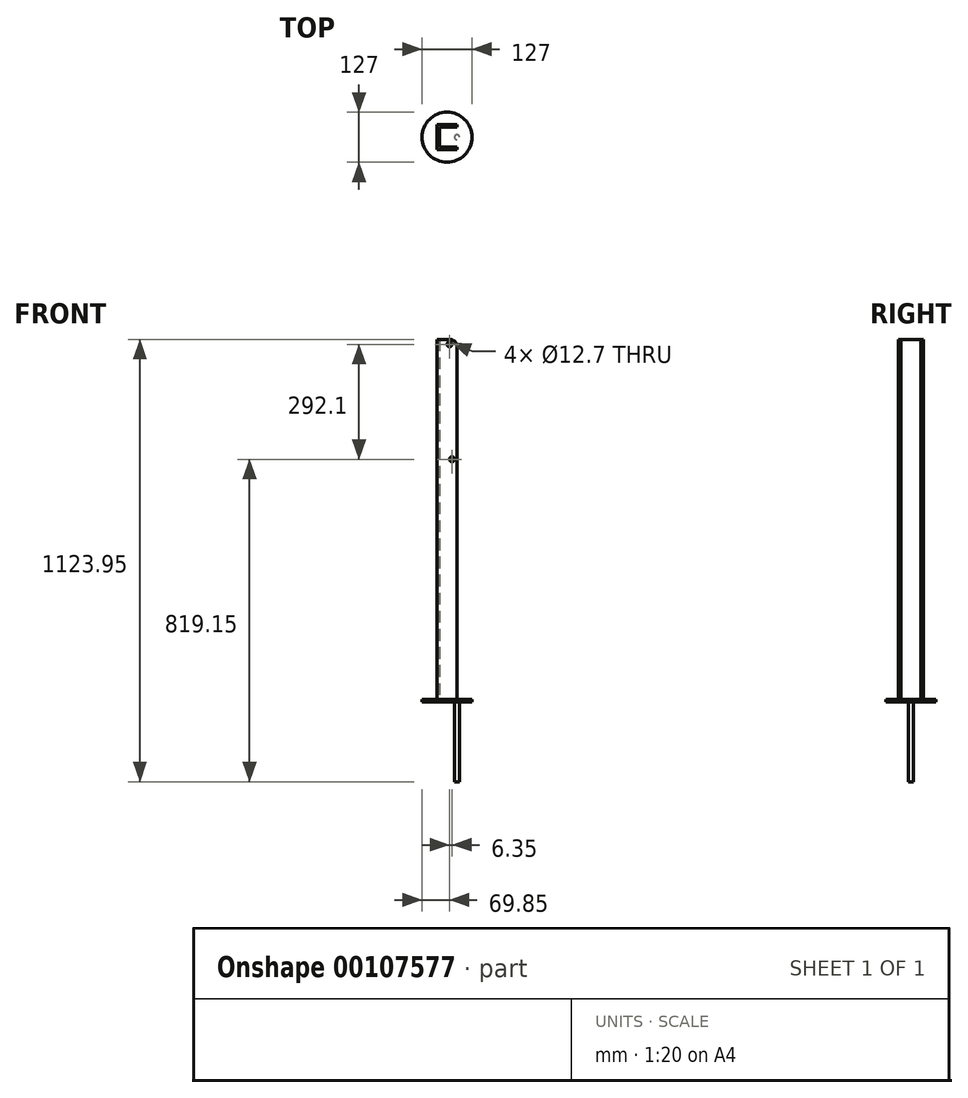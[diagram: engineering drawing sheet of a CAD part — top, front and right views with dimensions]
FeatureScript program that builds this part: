
annotation { "Feature Type Name" : "Feature", "Feature Type Description" : "" }
export const myFeature = defineFeature(function(context is Context, id is Id, definition is map)
    precondition{}
    {
        {
            var Q0;
            Q0=qCreatedBy(makeId("Top.planeOp"),FACE);
            var sketch = newSketch(context, id + "F0", { "sketchPlane" : qUnion([Q0])});
            skLineSegment(sketch, "E0.bottom", {"start": v(0, 31.75) * mm, "end": v(50.8, 31.75) * mm});
            skLineSegment(sketch, "E0.top", {"start": v(0, -31.75) * mm, "end": v(50.8, -31.75) * mm});
            skLineSegment(sketch, "E0.left", {"start": v(0, 31.75) * mm, "end": v(0, -31.75) * mm});
            skLineSegment(sketch, "E1.0", {"start": v(6.35, 25.4) * mm, "end": v(50.8, 25.4) * mm});
            skLineSegment(sketch, "E1.1", {"start": v(6.35, 25.4) * mm, "end": v(6.35, -25.4) * mm});
            skLineSegment(sketch, "E1.2", {"start": v(6.35, -25.4) * mm, "end": v(50.8, -25.4) * mm});
            skLineSegment(sketch, "E2", {"start": v(50.8, 31.75) * mm, "end": v(50.8, 25.4) * mm});
            skLineSegment(sketch, "E3", {"start": v(50.8, -25.4) * mm, "end": v(50.8, -31.75) * mm});
            skSolve(sketch);
        }
        {
            var Q0;
            Q0 = qSketchRegion(id + "F0", true);
            extrude(context, id + "F1", {"entities" : qUnion([Q0]), "depth" : 914.4 * mm});
        }
        {
            var Q0;
            Q0=makeQuery(id+"F1.opExtrude","SWEPT_FACE",FACE,{"disambiguationData":[OSD([sQuery(id+"F0.wireOp",EDGE,"E0.top")])]});
            var sketch = newSketch(context, id + "F2", { "sketchPlane" : qUnion([Q0])});
            skCircle(sketch, "E4", {"center": v(31.75, 901.7) * mm, "radius": 6.35 * mm});
            skCircle(sketch, "E5", {"center": v(38.1, 609.6) * mm, "radius": 6.35 * mm});
            skSolve(sketch);
        }
        {
            var Q0;
            Q0 = qSketchRegion(id + "F2", true);
            extrude(context, id + "F3", {"entities" : qUnion([Q0]), "operationType" : NewBodyOperationType.REMOVE, "endBound" : BoundingType.THROUGH_ALL, "oppositeDirection" : true, "depth" : 25.4 * mm});
        }
        {
            var Q0;
            Q0=makeQuery(id+"F1.opExtrude","CAP_EDGE",EDGE,{"disambiguationData":[OSD([sQuery(id+"F0.wireOp",EDGE,"E3")])],"isStart":false});
            var Q1;
            Q1=makeQuery(id+"F1.opExtrude","CAP_EDGE",EDGE,{"disambiguationData":[OSD([sQuery(id+"F0.wireOp",EDGE,"E2")])],"isStart":false});
            fillet(context, id + "F4", {"entities" : qUnion([Q0, Q1]), "radius" : 19.05 * mm, "tangentPropagation" : true, "allowEdgeOverflow" : false});
        }
        {
            var Q0;
            Q0=qCreatedBy(makeId("Top.planeOp"),FACE);
            var sketch = newSketch(context, id + "F5", { "sketchPlane" : qUnion([Q0])});
            skCircle(sketch, "E6", {"center": v(25.4, 0) * mm, "radius": 63.5 * mm});
            skSolve(sketch);
        }
        {
            var Q0;
            Q0 = qSketchRegion(id + "F5", true);
            extrude(context, id + "F6", {"entities" : qUnion([Q0]), "operationType" : NewBodyOperationType.ADD, "oppositeDirection" : true, "depth" : 6.35 * mm});
        }
        {
            var Q0;
            Q0=makeQuery(id+"F6.opExtrude","CAP_FACE",FACE,{"disambiguationData":[OSD([sQuery(id+"F5.wireOp",EDGE,"E6")])],"isStart":false});
            var sketch = newSketch(context, id + "F7", { "sketchPlane" : qUnion([Q0])});
            skCircle(sketch, "E7", {"center": v(50.8, 0) * mm, "radius": 6.35 * mm});
            skSolve(sketch);
        }
        {
            var Q0;
            Q0 = qSketchRegion(id + "F7", true);
            extrude(context, id + "F8", {"entities" : qUnion([Q0]), "operationType" : NewBodyOperationType.ADD, "depth" : 203.2 * mm});
        }
    });
